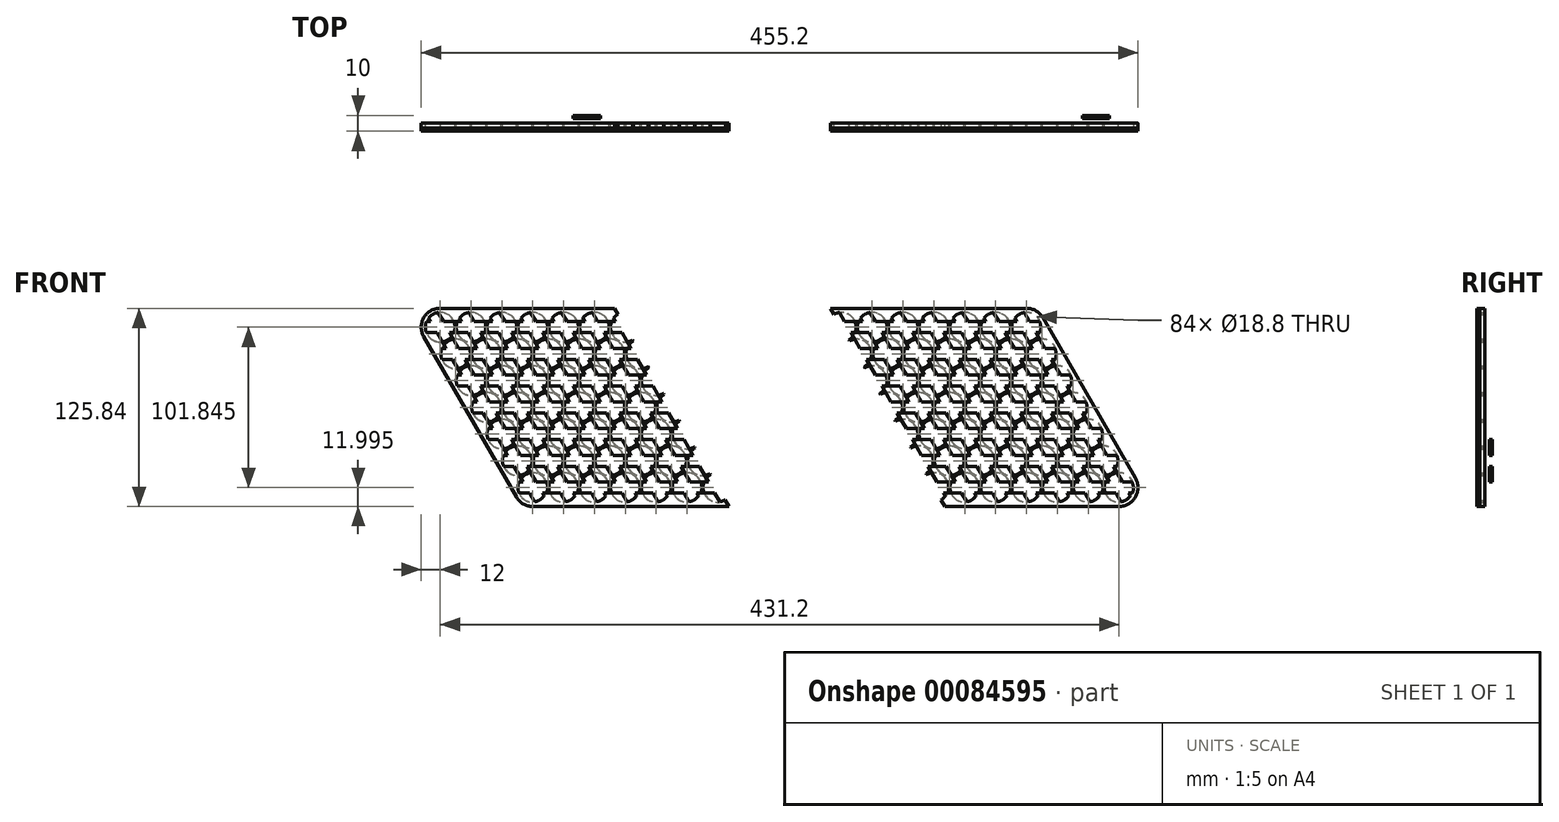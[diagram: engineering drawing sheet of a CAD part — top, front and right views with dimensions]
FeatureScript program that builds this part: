
annotation { "Feature Type Name" : "Feature", "Feature Type Description" : "" }
export const myFeature = defineFeature(function(context is Context, id is Id, definition is map)
    precondition{}
    {
        {
            var Q0;
            Q0=qCreatedBy(makeId("Front.planeOp"),FACE);
            var sketch = newSketch(context, id + "F0", { "sketchPlane" : qUnion([Q0]) });
            skLineSegment(sketch, "E0", {"start": v(0, 0) * mm, "end": v(79.44, 0) * mm, "construction": true});
            skLineSegment(sketch, "E1", {"start": v(0, 0) * mm, "end": v(43.4, -75.16) * mm, "construction": true});
            skCircle(sketch, "E2", {"center": v(0, 0) * mm, "radius": 9.4 * mm});
            skCircle(sketch, "E3.1.0.0", {"center": v(19.6, 0) * mm, "radius": 9.4 * mm});
            skCircle(sketch, "E3.2.0.0", {"center": v(39.2, 0) * mm, "radius": 9.4 * mm});
            skCircle(sketch, "E3.3.0.0", {"center": v(58.8, 0) * mm, "radius": 9.4 * mm});
            skCircle(sketch, "E3.4.0.0", {"center": v(78.4, 0) * mm, "radius": 9.4 * mm});
            skCircle(sketch, "E3.5.0.0", {"center": v(98, 0) * mm, "radius": 9.4 * mm});
            skCircle(sketch, "E3.6.0.0", {"center": v(117.6, 0) * mm, "radius": 9.4 * mm});
            skCircle(sketch, "E3.7.0.0", {"center": v(137.2, 0) * mm, "radius": 9.4 * mm});
            skCircle(sketch, "E3.8.0.0", {"center": v(156.8, 0) * mm, "radius": 9.4 * mm});
            skCircle(sketch, "E3.9.0.0", {"center": v(176.4, 0) * mm, "radius": 9.4 * mm});
            skCircle(sketch, "E3.10.0.0", {"center": v(196, 0) * mm, "radius": 9.4 * mm});
            skCircle(sketch, "E3.11.0.0", {"center": v(215.6, 0) * mm, "radius": 9.4 * mm});
            skCircle(sketch, "E3.12.0.0", {"center": v(235.2, 0) * mm, "radius": 9.4 * mm});
            skCircle(sketch, "E3.13.0.0", {"center": v(254.8, 0) * mm, "radius": 9.4 * mm});
            skCircle(sketch, "E3.14.0.0", {"center": v(274.4, 0) * mm, "radius": 9.4 * mm});
            skCircle(sketch, "E3.15.0.0", {"center": v(294, 0) * mm, "radius": 9.4 * mm});
            skCircle(sketch, "E3.16.0.0", {"center": v(313.6, 0) * mm, "radius": 9.4 * mm});
            skCircle(sketch, "E3.17.0.0", {"center": v(333.2, 0) * mm, "radius": 9.4 * mm});
            skCircle(sketch, "E3.18.0.0", {"center": v(352.8, 0) * mm, "radius": 9.4 * mm});
            skCircle(sketch, "E3.19.0.0", {"center": v(372.4, 0) * mm, "radius": 9.4 * mm});
            skLineSegment(sketch, "E3.direction1", {"start": v(0, 0) * mm, "end": v(19.6, 0) * mm, "construction": true});
            skCircle(sketch, "E4.1.0.0", {"center": v(9.8, -16.97) * mm, "radius": 9.4 * mm});
            skCircle(sketch, "E4.2.0.0", {"center": v(19.6, -33.95) * mm, "radius": 9.4 * mm});
            skCircle(sketch, "E4.3.0.0", {"center": v(29.4, -50.92) * mm, "radius": 9.4 * mm});
            skCircle(sketch, "E4.4.0.0", {"center": v(39.2, -67.9) * mm, "radius": 9.4 * mm});
            skCircle(sketch, "E4.5.0.0", {"center": v(49, -84.87) * mm, "radius": 9.4 * mm});
            skCircle(sketch, "E4.6.0.0", {"center": v(58.8, -101.84) * mm, "radius": 9.4 * mm});
            skLineSegment(sketch, "E4.direction1", {"start": v(0, 0) * mm, "end": v(9.8, -16.97) * mm, "construction": true});
            skCircle(sketch, "E5.1.0.0", {"center": v(29.4, -16.97) * mm, "radius": 9.4 * mm});
            skCircle(sketch, "E5.1.0.1", {"center": v(39.2, -33.95) * mm, "radius": 9.4 * mm});
            skCircle(sketch, "E5.1.0.2", {"center": v(49, -50.92) * mm, "radius": 9.4 * mm});
            skCircle(sketch, "E5.1.0.3", {"center": v(58.8, -67.9) * mm, "radius": 9.4 * mm});
            skCircle(sketch, "E5.1.0.4", {"center": v(68.6, -84.87) * mm, "radius": 9.4 * mm});
            skCircle(sketch, "E5.1.0.5", {"center": v(78.4, -101.84) * mm, "radius": 9.4 * mm});
            skCircle(sketch, "E5.2.0.0", {"center": v(49, -16.97) * mm, "radius": 9.4 * mm});
            skCircle(sketch, "E5.2.0.1", {"center": v(58.8, -33.95) * mm, "radius": 9.4 * mm});
            skCircle(sketch, "E5.2.0.2", {"center": v(68.6, -50.92) * mm, "radius": 9.4 * mm});
            skCircle(sketch, "E5.2.0.3", {"center": v(78.4, -67.9) * mm, "radius": 9.4 * mm});
            skCircle(sketch, "E5.2.0.4", {"center": v(88.2, -84.87) * mm, "radius": 9.4 * mm});
            skCircle(sketch, "E5.2.0.5", {"center": v(98, -101.84) * mm, "radius": 9.4 * mm});
            skCircle(sketch, "E5.3.0.0", {"center": v(68.6, -16.97) * mm, "radius": 9.4 * mm});
            skCircle(sketch, "E5.3.0.1", {"center": v(78.4, -33.95) * mm, "radius": 9.4 * mm});
            skCircle(sketch, "E5.3.0.2", {"center": v(88.2, -50.92) * mm, "radius": 9.4 * mm});
            skCircle(sketch, "E5.3.0.3", {"center": v(98, -67.9) * mm, "radius": 9.4 * mm});
            skCircle(sketch, "E5.3.0.4", {"center": v(107.8, -84.87) * mm, "radius": 9.4 * mm});
            skCircle(sketch, "E5.3.0.5", {"center": v(117.6, -101.84) * mm, "radius": 9.4 * mm});
            skCircle(sketch, "E5.4.0.0", {"center": v(88.2, -16.97) * mm, "radius": 9.4 * mm});
            skCircle(sketch, "E5.4.0.1", {"center": v(98, -33.95) * mm, "radius": 9.4 * mm});
            skCircle(sketch, "E5.4.0.2", {"center": v(107.8, -50.92) * mm, "radius": 9.4 * mm});
            skCircle(sketch, "E5.4.0.3", {"center": v(117.6, -67.9) * mm, "radius": 9.4 * mm});
            skCircle(sketch, "E5.4.0.4", {"center": v(127.4, -84.87) * mm, "radius": 9.4 * mm});
            skCircle(sketch, "E5.4.0.5", {"center": v(137.2, -101.84) * mm, "radius": 9.4 * mm});
            skCircle(sketch, "E5.5.0.0", {"center": v(107.8, -16.97) * mm, "radius": 9.4 * mm});
            skCircle(sketch, "E5.5.0.1", {"center": v(117.6, -33.95) * mm, "radius": 9.4 * mm});
            skCircle(sketch, "E5.5.0.2", {"center": v(127.4, -50.92) * mm, "radius": 9.4 * mm});
            skCircle(sketch, "E5.5.0.3", {"center": v(137.2, -67.9) * mm, "radius": 9.4 * mm});
            skCircle(sketch, "E5.5.0.4", {"center": v(147, -84.87) * mm, "radius": 9.4 * mm});
            skCircle(sketch, "E5.5.0.5", {"center": v(156.8, -101.84) * mm, "radius": 9.4 * mm});
            skCircle(sketch, "E5.6.0.0", {"center": v(127.4, -16.97) * mm, "radius": 9.4 * mm});
            skCircle(sketch, "E5.6.0.1", {"center": v(137.2, -33.95) * mm, "radius": 9.4 * mm});
            skCircle(sketch, "E5.6.0.2", {"center": v(147, -50.92) * mm, "radius": 9.4 * mm});
            skCircle(sketch, "E5.6.0.3", {"center": v(156.8, -67.9) * mm, "radius": 9.4 * mm});
            skCircle(sketch, "E5.6.0.4", {"center": v(166.6, -84.87) * mm, "radius": 9.4 * mm});
            skCircle(sketch, "E5.6.0.5", {"center": v(176.4, -101.84) * mm, "radius": 9.4 * mm});
            skCircle(sketch, "E5.7.0.0", {"center": v(147, -16.97) * mm, "radius": 9.4 * mm});
            skCircle(sketch, "E5.7.0.1", {"center": v(156.8, -33.95) * mm, "radius": 9.4 * mm});
            skCircle(sketch, "E5.7.0.2", {"center": v(166.6, -50.92) * mm, "radius": 9.4 * mm});
            skCircle(sketch, "E5.7.0.3", {"center": v(176.4, -67.9) * mm, "radius": 9.4 * mm});
            skCircle(sketch, "E5.7.0.4", {"center": v(186.2, -84.87) * mm, "radius": 9.4 * mm});
            skCircle(sketch, "E5.7.0.5", {"center": v(196, -101.84) * mm, "radius": 9.4 * mm});
            skCircle(sketch, "E5.8.0.0", {"center": v(166.6, -16.97) * mm, "radius": 9.4 * mm});
            skCircle(sketch, "E5.8.0.1", {"center": v(176.4, -33.95) * mm, "radius": 9.4 * mm});
            skCircle(sketch, "E5.8.0.2", {"center": v(186.2, -50.92) * mm, "radius": 9.4 * mm});
            skCircle(sketch, "E5.8.0.3", {"center": v(196, -67.9) * mm, "radius": 9.4 * mm});
            skCircle(sketch, "E5.8.0.4", {"center": v(205.8, -84.87) * mm, "radius": 9.4 * mm});
            skCircle(sketch, "E5.8.0.5", {"center": v(215.6, -101.84) * mm, "radius": 9.4 * mm});
            skCircle(sketch, "E5.9.0.0", {"center": v(186.2, -16.97) * mm, "radius": 9.4 * mm});
            skCircle(sketch, "E5.9.0.1", {"center": v(196, -33.95) * mm, "radius": 9.4 * mm});
            skCircle(sketch, "E5.9.0.2", {"center": v(205.8, -50.92) * mm, "radius": 9.4 * mm});
            skCircle(sketch, "E5.9.0.3", {"center": v(215.6, -67.9) * mm, "radius": 9.4 * mm});
            skCircle(sketch, "E5.9.0.4", {"center": v(225.4, -84.87) * mm, "radius": 9.4 * mm});
            skCircle(sketch, "E5.9.0.5", {"center": v(235.2, -101.84) * mm, "radius": 9.4 * mm});
            skCircle(sketch, "E5.10.0.0", {"center": v(205.8, -16.97) * mm, "radius": 9.4 * mm});
            skCircle(sketch, "E5.10.0.1", {"center": v(215.6, -33.95) * mm, "radius": 9.4 * mm});
            skCircle(sketch, "E5.10.0.2", {"center": v(225.4, -50.92) * mm, "radius": 9.4 * mm});
            skCircle(sketch, "E5.10.0.3", {"center": v(235.2, -67.9) * mm, "radius": 9.4 * mm});
            skCircle(sketch, "E5.10.0.4", {"center": v(245, -84.87) * mm, "radius": 9.4 * mm});
            skCircle(sketch, "E5.10.0.5", {"center": v(254.8, -101.84) * mm, "radius": 9.4 * mm});
            skCircle(sketch, "E5.11.0.0", {"center": v(225.4, -16.97) * mm, "radius": 9.4 * mm});
            skCircle(sketch, "E5.11.0.1", {"center": v(235.2, -33.95) * mm, "radius": 9.4 * mm});
            skCircle(sketch, "E5.11.0.2", {"center": v(245, -50.92) * mm, "radius": 9.4 * mm});
            skCircle(sketch, "E5.11.0.3", {"center": v(254.8, -67.9) * mm, "radius": 9.4 * mm});
            skCircle(sketch, "E5.11.0.4", {"center": v(264.6, -84.87) * mm, "radius": 9.4 * mm});
            skCircle(sketch, "E5.11.0.5", {"center": v(274.4, -101.84) * mm, "radius": 9.4 * mm});
            skCircle(sketch, "E5.12.0.0", {"center": v(245, -16.97) * mm, "radius": 9.4 * mm});
            skCircle(sketch, "E5.12.0.1", {"center": v(254.8, -33.95) * mm, "radius": 9.4 * mm});
            skCircle(sketch, "E5.12.0.2", {"center": v(264.6, -50.92) * mm, "radius": 9.4 * mm});
            skCircle(sketch, "E5.12.0.3", {"center": v(274.4, -67.9) * mm, "radius": 9.4 * mm});
            skCircle(sketch, "E5.12.0.4", {"center": v(284.2, -84.87) * mm, "radius": 9.4 * mm});
            skCircle(sketch, "E5.12.0.5", {"center": v(294, -101.84) * mm, "radius": 9.4 * mm});
            skCircle(sketch, "E5.13.0.0", {"center": v(264.6, -16.97) * mm, "radius": 9.4 * mm});
            skCircle(sketch, "E5.13.0.1", {"center": v(274.4, -33.95) * mm, "radius": 9.4 * mm});
            skCircle(sketch, "E5.13.0.2", {"center": v(284.2, -50.92) * mm, "radius": 9.4 * mm});
            skCircle(sketch, "E5.13.0.3", {"center": v(294, -67.9) * mm, "radius": 9.4 * mm});
            skCircle(sketch, "E5.13.0.4", {"center": v(303.8, -84.87) * mm, "radius": 9.4 * mm});
            skCircle(sketch, "E5.13.0.5", {"center": v(313.6, -101.84) * mm, "radius": 9.4 * mm});
            skCircle(sketch, "E5.14.0.0", {"center": v(284.2, -16.97) * mm, "radius": 9.4 * mm});
            skCircle(sketch, "E5.14.0.1", {"center": v(294, -33.95) * mm, "radius": 9.4 * mm});
            skCircle(sketch, "E5.14.0.2", {"center": v(303.8, -50.92) * mm, "radius": 9.4 * mm});
            skCircle(sketch, "E5.14.0.3", {"center": v(313.6, -67.9) * mm, "radius": 9.4 * mm});
            skCircle(sketch, "E5.14.0.4", {"center": v(323.4, -84.87) * mm, "radius": 9.4 * mm});
            skCircle(sketch, "E5.14.0.5", {"center": v(333.2, -101.84) * mm, "radius": 9.4 * mm});
            skCircle(sketch, "E5.15.0.0", {"center": v(303.8, -16.97) * mm, "radius": 9.4 * mm});
            skCircle(sketch, "E5.15.0.1", {"center": v(313.6, -33.95) * mm, "radius": 9.4 * mm});
            skCircle(sketch, "E5.15.0.2", {"center": v(323.4, -50.92) * mm, "radius": 9.4 * mm});
            skCircle(sketch, "E5.15.0.3", {"center": v(333.2, -67.9) * mm, "radius": 9.4 * mm});
            skCircle(sketch, "E5.15.0.4", {"center": v(343, -84.87) * mm, "radius": 9.4 * mm});
            skCircle(sketch, "E5.15.0.5", {"center": v(352.8, -101.84) * mm, "radius": 9.4 * mm});
            skCircle(sketch, "E5.16.0.0", {"center": v(323.4, -16.97) * mm, "radius": 9.4 * mm});
            skCircle(sketch, "E5.16.0.1", {"center": v(333.2, -33.95) * mm, "radius": 9.4 * mm});
            skCircle(sketch, "E5.16.0.2", {"center": v(343, -50.92) * mm, "radius": 9.4 * mm});
            skCircle(sketch, "E5.16.0.3", {"center": v(352.8, -67.9) * mm, "radius": 9.4 * mm});
            skCircle(sketch, "E5.16.0.4", {"center": v(362.6, -84.87) * mm, "radius": 9.4 * mm});
            skCircle(sketch, "E5.16.0.5", {"center": v(372.4, -101.84) * mm, "radius": 9.4 * mm});
            skCircle(sketch, "E5.17.0.0", {"center": v(343, -16.97) * mm, "radius": 9.4 * mm});
            skCircle(sketch, "E5.17.0.1", {"center": v(352.8, -33.95) * mm, "radius": 9.4 * mm});
            skCircle(sketch, "E5.17.0.2", {"center": v(362.6, -50.92) * mm, "radius": 9.4 * mm});
            skCircle(sketch, "E5.17.0.3", {"center": v(372.4, -67.9) * mm, "radius": 9.4 * mm});
            skCircle(sketch, "E5.17.0.4", {"center": v(382.2, -84.87) * mm, "radius": 9.4 * mm});
            skCircle(sketch, "E5.17.0.5", {"center": v(392, -101.84) * mm, "radius": 9.4 * mm});
            skCircle(sketch, "E5.18.0.0", {"center": v(362.6, -16.97) * mm, "radius": 9.4 * mm});
            skCircle(sketch, "E5.18.0.1", {"center": v(372.4, -33.95) * mm, "radius": 9.4 * mm});
            skCircle(sketch, "E5.18.0.2", {"center": v(382.2, -50.92) * mm, "radius": 9.4 * mm});
            skCircle(sketch, "E5.18.0.3", {"center": v(392, -67.9) * mm, "radius": 9.4 * mm});
            skCircle(sketch, "E5.18.0.4", {"center": v(401.8, -84.87) * mm, "radius": 9.4 * mm});
            skCircle(sketch, "E5.18.0.5", {"center": v(411.6, -101.84) * mm, "radius": 9.4 * mm});
            skCircle(sketch, "E5.19.0.0", {"center": v(382.2, -16.97) * mm, "radius": 9.4 * mm});
            skCircle(sketch, "E5.19.0.1", {"center": v(392, -33.95) * mm, "radius": 9.4 * mm});
            skCircle(sketch, "E5.19.0.2", {"center": v(401.8, -50.92) * mm, "radius": 9.4 * mm});
            skCircle(sketch, "E5.19.0.3", {"center": v(411.6, -67.9) * mm, "radius": 9.4 * mm});
            skCircle(sketch, "E5.19.0.4", {"center": v(421.4, -84.87) * mm, "radius": 9.4 * mm});
            skCircle(sketch, "E5.19.0.5", {"center": v(431.2, -101.84) * mm, "radius": 9.4 * mm});
            skLineSegment(sketch, "E5.direction1", {"start": v(9.8, -16.97) * mm, "end": v(29.4, -16.97) * mm, "construction": true});
            skLineSegment(sketch, "E6", {"start": v(0, 0) * mm, "end": v(372.4, 0) * mm, "construction": true});
            skLineSegment(sketch, "E7", {"start": v(372.4, 0) * mm, "end": v(441, -118.82) * mm, "construction": true});
            skLineSegment(sketch, "E8", {"start": v(441, -118.82) * mm, "end": v(68.6, -118.82) * mm, "construction": true});
            skLineSegment(sketch, "E9", {"start": v(68.6, -118.82) * mm, "end": v(0, 0) * mm, "construction": true});
            skArc(sketch, "E10", {"start": v(48.4, -107.84) * mm, "mid": v(52.8, -112.24) * mm, "end": v(58.8, -113.84) * mm});
            skArc(sketch, "E11", {"start": v(431.2, -113.84) * mm, "mid": v(441.6, -107.84) * mm, "end": v(441.6, -95.84) * mm});
            skArc(sketch, "E12", {"start": v(382.8, 6) * mm, "mid": v(378.4, 10.4) * mm, "end": v(372.4, 12) * mm});
            skArc(sketch, "E13", {"start": v(0, 12) * mm, "mid": v(-10.4, 6) * mm, "end": v(-10.4, -6) * mm});
            skLineSegment(sketch, "E14", {"start": v(0, 12) * mm, "end": v(372.4, 12) * mm});
            skLineSegment(sketch, "E15", {"start": v(-10.4, -6) * mm, "end": v(48.4, -107.84) * mm});
            skLineSegment(sketch, "E16", {"start": v(58.8, -113.84) * mm, "end": v(431.2, -113.84) * mm});
            skLineSegment(sketch, "E17", {"start": v(441.6, -95.84) * mm, "end": v(382.8, 6) * mm});
            skLineSegment(sketch, "E18", {"start": v(441.6, -107.84) * mm, "end": v(500.4, -6) * mm, "construction": true});
            skLineSegment(sketch, "E19", {"start": v(372.4, 12) * mm, "end": v(490, 12) * mm, "construction": true});
            skPoint(sketch, "E20.visualSharp", {"position": v(510.78, 12) * mm});
            skArc(sketch, "E20.filletArc", {"start": v(500.4, -6) * mm, "mid": v(500.4, 6) * mm, "end": v(490, 12) * mm, "construction": true});
            skSolve(sketch);
        }
        {
            var Q0;
            Q0=makeQuery(id+"F0.imprint","IMPRINT",FACE,{"disambiguationData":[TD([[makeQuery(id+"F0.imprint","IMPRINT",EDGE,{"derivedFrom":sQuery(id+"F0.wireOp",EDGE,"E2")}),-1.0]])]});
            extrude(context, id + "F1", {"entities" : qUnion([Q0]), "depth" : 3 * mm});
        }
        {
            var Q0;
            Q0=makeQuery(id+"F1.opExtrude","CAP_FACE",FACE,{"disambiguationData":[OSD([sQuery(id+"F0.wireOp",EDGE,"E2"),sQuery(id+"F0.wireOp",EDGE,"E3.1.0.0"),sQuery(id+"F0.wireOp",EDGE,"E3.2.0.0"),sQuery(id+"F0.wireOp",EDGE,"E3.3.0.0"),sQuery(id+"F0.wireOp",EDGE,"E3.4.0.0"),sQuery(id+"F0.wireOp",EDGE,"E3.5.0.0"),sQuery(id+"F0.wireOp",EDGE,"E3.6.0.0"),sQuery(id+"F0.wireOp",EDGE,"E3.7.0.0"),sQuery(id+"F0.wireOp",EDGE,"E3.8.0.0"),sQuery(id+"F0.wireOp",EDGE,"E3.9.0.0"),sQuery(id+"F0.wireOp",EDGE,"E3.10.0.0"),sQuery(id+"F0.wireOp",EDGE,"E3.11.0.0"),sQuery(id+"F0.wireOp",EDGE,"E3.12.0.0"),sQuery(id+"F0.wireOp",EDGE,"E3.13.0.0"),sQuery(id+"F0.wireOp",EDGE,"E3.14.0.0"),sQuery(id+"F0.wireOp",EDGE,"E3.15.0.0"),sQuery(id+"F0.wireOp",EDGE,"E3.16.0.0"),sQuery(id+"F0.wireOp",EDGE,"E3.17.0.0"),sQuery(id+"F0.wireOp",EDGE,"E3.18.0.0"),sQuery(id+"F0.wireOp",EDGE,"E3.19.0.0"),sQuery(id+"F0.wireOp",EDGE,"E4.1.0.0"),sQuery(id+"F0.wireOp",EDGE,"E4.2.0.0"),sQuery(id+"F0.wireOp",EDGE,"E4.3.0.0"),sQuery(id+"F0.wireOp",EDGE,"E4.4.0.0"),sQuery(id+"F0.wireOp",EDGE,"E4.5.0.0"),sQuery(id+"F0.wireOp",EDGE,"E4.6.0.0"),sQuery(id+"F0.wireOp",EDGE,"E5.1.0.0"),sQuery(id+"F0.wireOp",EDGE,"E5.1.0.1"),sQuery(id+"F0.wireOp",EDGE,"E5.1.0.2"),sQuery(id+"F0.wireOp",EDGE,"E5.1.0.3"),sQuery(id+"F0.wireOp",EDGE,"E5.1.0.4"),sQuery(id+"F0.wireOp",EDGE,"E5.1.0.5"),sQuery(id+"F0.wireOp",EDGE,"E5.2.0.0"),sQuery(id+"F0.wireOp",EDGE,"E5.2.0.1"),sQuery(id+"F0.wireOp",EDGE,"E5.2.0.2"),sQuery(id+"F0.wireOp",EDGE,"E5.2.0.3"),sQuery(id+"F0.wireOp",EDGE,"E5.2.0.4"),sQuery(id+"F0.wireOp",EDGE,"E5.2.0.5"),sQuery(id+"F0.wireOp",EDGE,"E5.3.0.0"),sQuery(id+"F0.wireOp",EDGE,"E5.3.0.1"),sQuery(id+"F0.wireOp",EDGE,"E5.3.0.2"),sQuery(id+"F0.wireOp",EDGE,"E5.3.0.3"),sQuery(id+"F0.wireOp",EDGE,"E5.3.0.4"),sQuery(id+"F0.wireOp",EDGE,"E5.3.0.5"),sQuery(id+"F0.wireOp",EDGE,"E5.4.0.0"),sQuery(id+"F0.wireOp",EDGE,"E5.4.0.1"),sQuery(id+"F0.wireOp",EDGE,"E5.4.0.2"),sQuery(id+"F0.wireOp",EDGE,"E5.4.0.3"),sQuery(id+"F0.wireOp",EDGE,"E5.4.0.4"),sQuery(id+"F0.wireOp",EDGE,"E5.4.0.5"),sQuery(id+"F0.wireOp",EDGE,"E5.5.0.0"),sQuery(id+"F0.wireOp",EDGE,"E5.5.0.1"),sQuery(id+"F0.wireOp",EDGE,"E5.5.0.2"),sQuery(id+"F0.wireOp",EDGE,"E5.5.0.3"),sQuery(id+"F0.wireOp",EDGE,"E5.5.0.4"),sQuery(id+"F0.wireOp",EDGE,"E5.5.0.5"),sQuery(id+"F0.wireOp",EDGE,"E5.6.0.0"),sQuery(id+"F0.wireOp",EDGE,"E5.6.0.1"),sQuery(id+"F0.wireOp",EDGE,"E5.6.0.2"),sQuery(id+"F0.wireOp",EDGE,"E5.6.0.3"),sQuery(id+"F0.wireOp",EDGE,"E5.6.0.4"),sQuery(id+"F0.wireOp",EDGE,"E5.6.0.5"),sQuery(id+"F0.wireOp",EDGE,"E5.7.0.0"),sQuery(id+"F0.wireOp",EDGE,"E5.7.0.1"),sQuery(id+"F0.wireOp",EDGE,"E5.7.0.2"),sQuery(id+"F0.wireOp",EDGE,"E5.7.0.3"),sQuery(id+"F0.wireOp",EDGE,"E5.7.0.4"),sQuery(id+"F0.wireOp",EDGE,"E5.7.0.5"),sQuery(id+"F0.wireOp",EDGE,"E5.8.0.0"),sQuery(id+"F0.wireOp",EDGE,"E5.8.0.1"),sQuery(id+"F0.wireOp",EDGE,"E5.8.0.2"),sQuery(id+"F0.wireOp",EDGE,"E5.8.0.3"),sQuery(id+"F0.wireOp",EDGE,"E5.8.0.4"),sQuery(id+"F0.wireOp",EDGE,"E5.8.0.5"),sQuery(id+"F0.wireOp",EDGE,"E5.9.0.0"),sQuery(id+"F0.wireOp",EDGE,"E5.9.0.1"),sQuery(id+"F0.wireOp",EDGE,"E5.9.0.2"),sQuery(id+"F0.wireOp",EDGE,"E5.9.0.3"),sQuery(id+"F0.wireOp",EDGE,"E5.9.0.4"),sQuery(id+"F0.wireOp",EDGE,"E5.9.0.5"),sQuery(id+"F0.wireOp",EDGE,"E5.10.0.0"),sQuery(id+"F0.wireOp",EDGE,"E5.10.0.1"),sQuery(id+"F0.wireOp",EDGE,"E5.10.0.2"),sQuery(id+"F0.wireOp",EDGE,"E5.10.0.3"),sQuery(id+"F0.wireOp",EDGE,"E5.10.0.4"),sQuery(id+"F0.wireOp",EDGE,"E5.10.0.5"),sQuery(id+"F0.wireOp",EDGE,"E5.11.0.0"),sQuery(id+"F0.wireOp",EDGE,"E5.11.0.1"),sQuery(id+"F0.wireOp",EDGE,"E5.11.0.2"),sQuery(id+"F0.wireOp",EDGE,"E5.11.0.3"),sQuery(id+"F0.wireOp",EDGE,"E5.11.0.4"),sQuery(id+"F0.wireOp",EDGE,"E5.11.0.5"),sQuery(id+"F0.wireOp",EDGE,"E5.12.0.0"),sQuery(id+"F0.wireOp",EDGE,"E5.12.0.1"),sQuery(id+"F0.wireOp",EDGE,"E5.12.0.2"),sQuery(id+"F0.wireOp",EDGE,"E5.12.0.3"),sQuery(id+"F0.wireOp",EDGE,"E5.12.0.4"),sQuery(id+"F0.wireOp",EDGE,"E5.12.0.5"),sQuery(id+"F0.wireOp",EDGE,"E5.13.0.0"),sQuery(id+"F0.wireOp",EDGE,"E5.13.0.1"),sQuery(id+"F0.wireOp",EDGE,"E5.13.0.2"),sQuery(id+"F0.wireOp",EDGE,"E5.13.0.3"),sQuery(id+"F0.wireOp",EDGE,"E5.13.0.4"),sQuery(id+"F0.wireOp",EDGE,"E5.13.0.5"),sQuery(id+"F0.wireOp",EDGE,"E5.14.0.0"),sQuery(id+"F0.wireOp",EDGE,"E5.14.0.1"),sQuery(id+"F0.wireOp",EDGE,"E5.14.0.2"),sQuery(id+"F0.wireOp",EDGE,"E5.14.0.3"),sQuery(id+"F0.wireOp",EDGE,"E5.14.0.4"),sQuery(id+"F0.wireOp",EDGE,"E5.14.0.5"),sQuery(id+"F0.wireOp",EDGE,"E5.15.0.0"),sQuery(id+"F0.wireOp",EDGE,"E5.15.0.1"),sQuery(id+"F0.wireOp",EDGE,"E5.15.0.2"),sQuery(id+"F0.wireOp",EDGE,"E5.15.0.3"),sQuery(id+"F0.wireOp",EDGE,"E5.15.0.4"),sQuery(id+"F0.wireOp",EDGE,"E5.15.0.5"),sQuery(id+"F0.wireOp",EDGE,"E5.16.0.0"),sQuery(id+"F0.wireOp",EDGE,"E5.16.0.1"),sQuery(id+"F0.wireOp",EDGE,"E5.16.0.2"),sQuery(id+"F0.wireOp",EDGE,"E5.16.0.3"),sQuery(id+"F0.wireOp",EDGE,"E5.16.0.4"),sQuery(id+"F0.wireOp",EDGE,"E5.16.0.5"),sQuery(id+"F0.wireOp",EDGE,"E5.17.0.0"),sQuery(id+"F0.wireOp",EDGE,"E5.17.0.1"),sQuery(id+"F0.wireOp",EDGE,"E5.17.0.2"),sQuery(id+"F0.wireOp",EDGE,"E5.17.0.3"),sQuery(id+"F0.wireOp",EDGE,"E5.17.0.4"),sQuery(id+"F0.wireOp",EDGE,"E5.17.0.5"),sQuery(id+"F0.wireOp",EDGE,"E5.18.0.0"),sQuery(id+"F0.wireOp",EDGE,"E5.18.0.1"),sQuery(id+"F0.wireOp",EDGE,"E5.18.0.2"),sQuery(id+"F0.wireOp",EDGE,"E5.18.0.3"),sQuery(id+"F0.wireOp",EDGE,"E5.18.0.4"),sQuery(id+"F0.wireOp",EDGE,"E5.18.0.5"),sQuery(id+"F0.wireOp",EDGE,"E5.19.0.0"),sQuery(id+"F0.wireOp",EDGE,"E5.19.0.1"),sQuery(id+"F0.wireOp",EDGE,"E5.19.0.2"),sQuery(id+"F0.wireOp",EDGE,"E5.19.0.3"),sQuery(id+"F0.wireOp",EDGE,"E5.19.0.4"),sQuery(id+"F0.wireOp",EDGE,"E5.19.0.5"),sQuery(id+"F0.wireOp",EDGE,"E10"),sQuery(id+"F0.wireOp",EDGE,"E11"),sQuery(id+"F0.wireOp",EDGE,"E12"),sQuery(id+"F0.wireOp",EDGE,"E13"),sQuery(id+"F0.wireOp",EDGE,"E14"),sQuery(id+"F0.wireOp",EDGE,"E15"),sQuery(id+"F0.wireOp",EDGE,"E16"),sQuery(id+"F0.wireOp",EDGE,"E17")])],"isStart":false});
            var sketch = newSketch(context, id + "F2", { "sketchPlane" : qUnion([Q0]) });
            skLineSegment(sketch, "E21.0", {"start": v(0, 12) * mm, "end": v(372.4, 12) * mm});
            skArc(sketch, "E21.1", {"start": v(0, 12) * mm, "mid": v(-10.4, 6) * mm, "end": v(-10.4, -6) * mm});
            skLineSegment(sketch, "E21.2", {"start": v(-10.4, -6) * mm, "end": v(48.4, -107.84) * mm});
            skArc(sketch, "E21.3", {"start": v(382.8, 6) * mm, "mid": v(378.4, 10.4) * mm, "end": v(372.4, 12) * mm});
            skLineSegment(sketch, "E21.4", {"start": v(441.6, -95.84) * mm, "end": v(382.8, 6) * mm});
            skArc(sketch, "E21.5", {"start": v(431.2, -113.84) * mm, "mid": v(441.6, -107.84) * mm, "end": v(441.6, -95.84) * mm});
            skLineSegment(sketch, "E21.6", {"start": v(58.8, -113.84) * mm, "end": v(431.2, -113.84) * mm});
            skArc(sketch, "E21.7", {"start": v(48.4, -107.84) * mm, "mid": v(52.8, -112.24) * mm, "end": v(58.8, -113.84) * mm});
            skSolve(sketch);
        }
        {
            var Q0;
            Q0=qSketchRegion(id+"F2",true);
            extrude(context, id + "F3", {"entities" : qUnion([Q0]), "depth" : 2 * mm});
        }
        {
            var Q0;
            Q0=makeQuery(id+"F3.opExtrude","CAP_FACE",FACE,{"disambiguationData":[OSD([sQuery(id+"F2.wireOp",EDGE,"E21.0"),sQuery(id+"F2.wireOp",EDGE,"E21.1"),sQuery(id+"F2.wireOp",EDGE,"E21.2"),sQuery(id+"F2.wireOp",EDGE,"E21.3"),sQuery(id+"F2.wireOp",EDGE,"E21.4"),sQuery(id+"F2.wireOp",EDGE,"E21.5"),sQuery(id+"F2.wireOp",EDGE,"E21.6"),sQuery(id+"F2.wireOp",EDGE,"E21.7")])],"isStart":false});
            var sketch = newSketch(context, id + "F4", { "sketchPlane" : qUnion([Q0]) });
            skLineSegment(sketch, "E22", {"start": v(0, 0) * mm, "end": v(58.8, -101.84) * mm, "construction": true});
            skLineSegment(sketch, "E23", {"start": v(58.8, -101.84) * mm, "end": v(431.2, -101.84) * mm, "construction": true});
            skLineSegment(sketch, "E24", {"start": v(431.2, -101.84) * mm, "end": v(372.4, 0) * mm, "construction": true});
            skLineSegment(sketch, "E25", {"start": v(372.4, 0) * mm, "end": v(0, 0) * mm, "construction": true});
            skLineSegment(sketch, "E26", {"start": v(-8.72, 3.5) * mm, "end": v(380.69, 3.5) * mm});
            skLineSegment(sketch, "E27.MirrorCS", {"start": v(-8.72, -3.5) * mm, "end": v(380.9, -3.5) * mm});
            skArc(sketch, "E28.0", {"start": v(-8.72, 3.5) * mm, "mid": v(-9.4, 0) * mm, "end": v(-8.72, -3.5) * mm});
            skArc(sketch, "E29.trimOffspring", {"start": v(380.9, -3.5) * mm, "mid": v(381.47, 0.02) * mm, "end": v(380.69, 3.5) * mm});
            skPoint(sketch, "E30.orphan", {"position": v(456.43, 3.5) * mm});
            skPoint(sketch, "E31.orphan", {"position": v(456.43, -3.5) * mm});
            skPoint(sketch, "E32.orphan", {"position": v(-45.25, 3.5) * mm});
            skPoint(sketch, "E33.orphan", {"position": v(-45.25, -3.5) * mm});
            skLineSegment(sketch, "E34.0.1.0", {"start": v(1.08, -13.47) * mm, "end": v(390.49, -13.47) * mm});
            skLineSegment(sketch, "E34.0.1.1", {"start": v(1.08, -20.47) * mm, "end": v(390.7, -20.47) * mm});
            skArc(sketch, "E34.0.1.2", {"start": v(1.08, -13.47) * mm, "mid": v(0.4, -16.97) * mm, "end": v(1.08, -20.47) * mm});
            skArc(sketch, "E34.0.1.3", {"start": v(390.7, -20.47) * mm, "mid": v(391.27, -16.95) * mm, "end": v(390.49, -13.47) * mm});
            skLineSegment(sketch, "E34.0.2.0", {"start": v(10.88, -30.45) * mm, "end": v(400.29, -30.45) * mm});
            skLineSegment(sketch, "E34.0.2.1", {"start": v(10.88, -37.45) * mm, "end": v(400.5, -37.45) * mm});
            skArc(sketch, "E34.0.2.2", {"start": v(10.88, -30.45) * mm, "mid": v(10.2, -33.95) * mm, "end": v(10.88, -37.45) * mm});
            skArc(sketch, "E34.0.2.3", {"start": v(400.5, -37.45) * mm, "mid": v(401.07, -33.93) * mm, "end": v(400.29, -30.45) * mm});
            skLineSegment(sketch, "E34.0.3.0", {"start": v(20.68, -47.42) * mm, "end": v(410.09, -47.42) * mm});
            skLineSegment(sketch, "E34.0.3.1", {"start": v(20.68, -54.42) * mm, "end": v(410.3, -54.42) * mm});
            skArc(sketch, "E34.0.3.2", {"start": v(20.68, -47.42) * mm, "mid": v(20, -50.92) * mm, "end": v(20.68, -54.42) * mm});
            skArc(sketch, "E34.0.3.3", {"start": v(410.3, -54.42) * mm, "mid": v(410.87, -50.9) * mm, "end": v(410.09, -47.42) * mm});
            skLineSegment(sketch, "E34.0.4.0", {"start": v(30.48, -64.4) * mm, "end": v(419.89, -64.4) * mm});
            skLineSegment(sketch, "E34.0.4.1", {"start": v(30.48, -71.4) * mm, "end": v(420.1, -71.4) * mm});
            skArc(sketch, "E34.0.4.2", {"start": v(30.48, -64.4) * mm, "mid": v(29.8, -67.9) * mm, "end": v(30.48, -71.4) * mm});
            skArc(sketch, "E34.0.4.3", {"start": v(420.1, -71.4) * mm, "mid": v(420.67, -67.88) * mm, "end": v(419.89, -64.4) * mm});
            skLineSegment(sketch, "E34.0.5.0", {"start": v(40.28, -81.37) * mm, "end": v(429.69, -81.37) * mm});
            skLineSegment(sketch, "E34.0.5.1", {"start": v(40.28, -88.37) * mm, "end": v(429.9, -88.37) * mm});
            skArc(sketch, "E34.0.5.2", {"start": v(40.28, -81.37) * mm, "mid": v(39.6, -84.87) * mm, "end": v(40.28, -88.37) * mm});
            skArc(sketch, "E34.0.5.3", {"start": v(429.9, -88.37) * mm, "mid": v(430.47, -84.85) * mm, "end": v(429.69, -81.37) * mm});
            skLineSegment(sketch, "E34.0.6.0", {"start": v(50.08, -98.34) * mm, "end": v(439.49, -98.34) * mm});
            skLineSegment(sketch, "E34.0.6.1", {"start": v(50.08, -105.34) * mm, "end": v(439.7, -105.34) * mm});
            skArc(sketch, "E34.0.6.2", {"start": v(50.08, -98.34) * mm, "mid": v(49.4, -101.84) * mm, "end": v(50.08, -105.34) * mm});
            skArc(sketch, "E34.0.6.3", {"start": v(439.7, -105.34) * mm, "mid": v(440.27, -101.82) * mm, "end": v(439.49, -98.34) * mm});
            skLineSegment(sketch, "E34.direction1", {"start": v(-8.72, 3.5) * mm, "end": v(16.28, 3.5) * mm, "construction": true});
            skLineSegment(sketch, "E34.direction2", {"start": v(-8.72, 3.5) * mm, "end": v(1.08, -13.47) * mm, "construction": true});
            skSolve(sketch);
        }
        {
            var Q0;
            Q0=qSketchRegion(id+"F4",true);
            extrude(context, id + "F5", {"entities" : qUnion([Q0]), "operationType" : NewBodyOperationType.REMOVE, "endBound" : BoundingType.UP_TO_NEXT, "oppositeDirection" : true, "depth" : 25 * mm});
        }
        {
            var Q0;
            Q0=makeQuery(id+"F3.opExtrude","CAP_FACE",FACE,{"disambiguationData":[OSD([sQuery(id+"F2.wireOp",EDGE,"E21.0"),sQuery(id+"F2.wireOp",EDGE,"E21.1"),sQuery(id+"F2.wireOp",EDGE,"E21.2"),sQuery(id+"F2.wireOp",EDGE,"E21.3"),sQuery(id+"F2.wireOp",EDGE,"E21.4"),sQuery(id+"F2.wireOp",EDGE,"E21.5"),sQuery(id+"F2.wireOp",EDGE,"E21.6"),sQuery(id+"F2.wireOp",EDGE,"E21.7")])],"isStart":false});
            var sketch = newSketch(context, id + "F6", { "sketchPlane" : qUnion([Q0]) });
            skLineSegment(sketch, "E35", {"start": v(0, 0) * mm, "end": v(58.8, -101.84) * mm, "construction": true});
            skLineSegment(sketch, "E36", {"start": v(-1.33, 9.3) * mm, "end": v(65.94, -107.21) * mm});
            skLineSegment(sketch, "E37.MirrorCS", {"start": v(-7.4, 5.8) * mm, "end": v(60.02, -110.96) * mm});
            skArc(sketch, "E38.0", {"start": v(-1.33, 9.3) * mm, "mid": v(-4.7, 8.14) * mm, "end": v(-7.4, 5.8) * mm});
            skArc(sketch, "E39.trimOffspring", {"start": v(60.02, -110.96) * mm, "mid": v(63.34, -109.66) * mm, "end": v(65.94, -107.21) * mm});
            skPoint(sketch, "E40.orphan", {"position": v(72.39, -132.38) * mm});
            skPoint(sketch, "E41.orphan", {"position": v(78.45, -128.88) * mm});
            skPoint(sketch, "E42.orphan", {"position": v(-7.3, 19.64) * mm});
            skPoint(sketch, "E43.orphan", {"position": v(-13.36, 16.14) * mm});
            skArc(sketch, "E44.1.0.0", {"start": v(18.27, 9.3) * mm, "mid": v(14.9, 8.14) * mm, "end": v(12.2, 5.8) * mm});
            skLineSegment(sketch, "E44.1.0.1", {"start": v(12.2, 5.8) * mm, "end": v(79.62, -110.96) * mm});
            skLineSegment(sketch, "E44.1.0.2", {"start": v(18.27, 9.3) * mm, "end": v(85.54, -107.21) * mm});
            skArc(sketch, "E44.1.0.3", {"start": v(79.62, -110.96) * mm, "mid": v(82.94, -109.66) * mm, "end": v(85.54, -107.21) * mm});
            skArc(sketch, "E44.2.0.0", {"start": v(37.87, 9.3) * mm, "mid": v(34.5, 8.14) * mm, "end": v(31.8, 5.8) * mm});
            skLineSegment(sketch, "E44.2.0.1", {"start": v(31.8, 5.8) * mm, "end": v(99.22, -110.96) * mm});
            skLineSegment(sketch, "E44.2.0.2", {"start": v(37.87, 9.3) * mm, "end": v(105.14, -107.21) * mm});
            skArc(sketch, "E44.2.0.3", {"start": v(99.22, -110.96) * mm, "mid": v(102.54, -109.66) * mm, "end": v(105.14, -107.21) * mm});
            skArc(sketch, "E44.3.0.0", {"start": v(57.47, 9.3) * mm, "mid": v(54.1, 8.14) * mm, "end": v(51.4, 5.8) * mm});
            skLineSegment(sketch, "E44.3.0.1", {"start": v(51.4, 5.8) * mm, "end": v(118.82, -110.96) * mm});
            skLineSegment(sketch, "E44.3.0.2", {"start": v(57.47, 9.3) * mm, "end": v(124.74, -107.21) * mm});
            skArc(sketch, "E44.3.0.3", {"start": v(118.82, -110.96) * mm, "mid": v(122.14, -109.66) * mm, "end": v(124.74, -107.21) * mm});
            skArc(sketch, "E44.4.0.0", {"start": v(77.07, 9.3) * mm, "mid": v(73.7, 8.14) * mm, "end": v(71, 5.8) * mm});
            skLineSegment(sketch, "E44.4.0.1", {"start": v(71, 5.8) * mm, "end": v(138.42, -110.96) * mm});
            skLineSegment(sketch, "E44.4.0.2", {"start": v(77.07, 9.3) * mm, "end": v(144.34, -107.21) * mm});
            skArc(sketch, "E44.4.0.3", {"start": v(138.42, -110.96) * mm, "mid": v(141.74, -109.66) * mm, "end": v(144.34, -107.21) * mm});
            skArc(sketch, "E44.5.0.0", {"start": v(96.67, 9.3) * mm, "mid": v(93.3, 8.14) * mm, "end": v(90.6, 5.8) * mm});
            skLineSegment(sketch, "E44.5.0.1", {"start": v(90.6, 5.8) * mm, "end": v(158.02, -110.96) * mm});
            skLineSegment(sketch, "E44.5.0.2", {"start": v(96.67, 9.3) * mm, "end": v(163.94, -107.21) * mm});
            skArc(sketch, "E44.5.0.3", {"start": v(158.02, -110.96) * mm, "mid": v(161.34, -109.66) * mm, "end": v(163.94, -107.21) * mm});
            skArc(sketch, "E44.6.0.0", {"start": v(116.27, 9.3) * mm, "mid": v(112.9, 8.14) * mm, "end": v(110.2, 5.8) * mm});
            skLineSegment(sketch, "E44.6.0.1", {"start": v(110.2, 5.8) * mm, "end": v(177.62, -110.96) * mm});
            skLineSegment(sketch, "E44.6.0.2", {"start": v(116.27, 9.3) * mm, "end": v(183.54, -107.21) * mm});
            skArc(sketch, "E44.6.0.3", {"start": v(177.62, -110.96) * mm, "mid": v(180.94, -109.66) * mm, "end": v(183.54, -107.21) * mm});
            skArc(sketch, "E44.7.0.0", {"start": v(135.87, 9.3) * mm, "mid": v(132.5, 8.14) * mm, "end": v(129.8, 5.8) * mm});
            skLineSegment(sketch, "E44.7.0.1", {"start": v(129.8, 5.8) * mm, "end": v(197.22, -110.96) * mm});
            skLineSegment(sketch, "E44.7.0.2", {"start": v(135.87, 9.3) * mm, "end": v(203.14, -107.21) * mm});
            skArc(sketch, "E44.7.0.3", {"start": v(197.22, -110.96) * mm, "mid": v(200.54, -109.66) * mm, "end": v(203.14, -107.21) * mm});
            skArc(sketch, "E44.8.0.0", {"start": v(155.47, 9.3) * mm, "mid": v(152.1, 8.14) * mm, "end": v(149.4, 5.8) * mm});
            skLineSegment(sketch, "E44.8.0.1", {"start": v(149.4, 5.8) * mm, "end": v(216.82, -110.96) * mm});
            skLineSegment(sketch, "E44.8.0.2", {"start": v(155.47, 9.3) * mm, "end": v(222.74, -107.21) * mm});
            skArc(sketch, "E44.8.0.3", {"start": v(216.82, -110.96) * mm, "mid": v(220.14, -109.66) * mm, "end": v(222.74, -107.21) * mm});
            skArc(sketch, "E44.9.0.0", {"start": v(175.07, 9.3) * mm, "mid": v(171.7, 8.14) * mm, "end": v(169, 5.8) * mm});
            skLineSegment(sketch, "E44.9.0.1", {"start": v(169, 5.8) * mm, "end": v(236.42, -110.96) * mm});
            skLineSegment(sketch, "E44.9.0.2", {"start": v(175.07, 9.3) * mm, "end": v(242.34, -107.21) * mm});
            skArc(sketch, "E44.9.0.3", {"start": v(236.42, -110.96) * mm, "mid": v(239.74, -109.66) * mm, "end": v(242.34, -107.21) * mm});
            skArc(sketch, "E44.10.0.0", {"start": v(194.67, 9.3) * mm, "mid": v(191.3, 8.14) * mm, "end": v(188.6, 5.8) * mm});
            skLineSegment(sketch, "E44.10.0.1", {"start": v(188.6, 5.8) * mm, "end": v(256.02, -110.96) * mm});
            skLineSegment(sketch, "E44.10.0.2", {"start": v(194.67, 9.3) * mm, "end": v(261.94, -107.21) * mm});
            skArc(sketch, "E44.10.0.3", {"start": v(256.02, -110.96) * mm, "mid": v(259.34, -109.66) * mm, "end": v(261.94, -107.21) * mm});
            skArc(sketch, "E44.11.0.0", {"start": v(214.27, 9.3) * mm, "mid": v(210.9, 8.14) * mm, "end": v(208.2, 5.8) * mm});
            skLineSegment(sketch, "E44.11.0.1", {"start": v(208.2, 5.8) * mm, "end": v(275.62, -110.96) * mm});
            skLineSegment(sketch, "E44.11.0.2", {"start": v(214.27, 9.3) * mm, "end": v(281.54, -107.21) * mm});
            skArc(sketch, "E44.11.0.3", {"start": v(275.62, -110.96) * mm, "mid": v(278.94, -109.66) * mm, "end": v(281.54, -107.21) * mm});
            skArc(sketch, "E44.12.0.0", {"start": v(233.87, 9.3) * mm, "mid": v(230.5, 8.14) * mm, "end": v(227.8, 5.8) * mm});
            skLineSegment(sketch, "E44.12.0.1", {"start": v(227.8, 5.8) * mm, "end": v(295.22, -110.96) * mm});
            skLineSegment(sketch, "E44.12.0.2", {"start": v(233.87, 9.3) * mm, "end": v(301.14, -107.21) * mm});
            skArc(sketch, "E44.12.0.3", {"start": v(295.22, -110.96) * mm, "mid": v(298.54, -109.66) * mm, "end": v(301.14, -107.21) * mm});
            skArc(sketch, "E44.13.0.0", {"start": v(253.47, 9.3) * mm, "mid": v(250.1, 8.14) * mm, "end": v(247.4, 5.8) * mm});
            skLineSegment(sketch, "E44.13.0.1", {"start": v(247.4, 5.8) * mm, "end": v(314.82, -110.96) * mm});
            skLineSegment(sketch, "E44.13.0.2", {"start": v(253.47, 9.3) * mm, "end": v(320.74, -107.21) * mm});
            skArc(sketch, "E44.13.0.3", {"start": v(314.82, -110.96) * mm, "mid": v(318.14, -109.66) * mm, "end": v(320.74, -107.21) * mm});
            skArc(sketch, "E44.14.0.0", {"start": v(273.07, 9.3) * mm, "mid": v(269.7, 8.14) * mm, "end": v(267, 5.8) * mm});
            skLineSegment(sketch, "E44.14.0.1", {"start": v(267, 5.8) * mm, "end": v(334.42, -110.96) * mm});
            skLineSegment(sketch, "E44.14.0.2", {"start": v(273.07, 9.3) * mm, "end": v(340.34, -107.21) * mm});
            skArc(sketch, "E44.14.0.3", {"start": v(334.42, -110.96) * mm, "mid": v(337.74, -109.66) * mm, "end": v(340.34, -107.21) * mm});
            skArc(sketch, "E44.15.0.0", {"start": v(292.67, 9.3) * mm, "mid": v(289.3, 8.14) * mm, "end": v(286.6, 5.8) * mm});
            skLineSegment(sketch, "E44.15.0.1", {"start": v(286.6, 5.8) * mm, "end": v(354.02, -110.96) * mm});
            skLineSegment(sketch, "E44.15.0.2", {"start": v(292.67, 9.3) * mm, "end": v(359.94, -107.21) * mm});
            skArc(sketch, "E44.15.0.3", {"start": v(354.02, -110.96) * mm, "mid": v(357.34, -109.66) * mm, "end": v(359.94, -107.21) * mm});
            skArc(sketch, "E44.16.0.0", {"start": v(312.27, 9.3) * mm, "mid": v(308.9, 8.14) * mm, "end": v(306.2, 5.8) * mm});
            skLineSegment(sketch, "E44.16.0.1", {"start": v(306.2, 5.8) * mm, "end": v(373.62, -110.96) * mm});
            skLineSegment(sketch, "E44.16.0.2", {"start": v(312.27, 9.3) * mm, "end": v(379.54, -107.21) * mm});
            skArc(sketch, "E44.16.0.3", {"start": v(373.62, -110.96) * mm, "mid": v(376.94, -109.66) * mm, "end": v(379.54, -107.21) * mm});
            skArc(sketch, "E44.17.0.0", {"start": v(331.87, 9.3) * mm, "mid": v(328.5, 8.14) * mm, "end": v(325.8, 5.8) * mm});
            skLineSegment(sketch, "E44.17.0.1", {"start": v(325.8, 5.8) * mm, "end": v(393.22, -110.96) * mm});
            skLineSegment(sketch, "E44.17.0.2", {"start": v(331.87, 9.3) * mm, "end": v(399.14, -107.21) * mm});
            skArc(sketch, "E44.17.0.3", {"start": v(393.22, -110.96) * mm, "mid": v(396.54, -109.66) * mm, "end": v(399.14, -107.21) * mm});
            skArc(sketch, "E44.18.0.0", {"start": v(351.47, 9.3) * mm, "mid": v(348.1, 8.14) * mm, "end": v(345.4, 5.8) * mm});
            skLineSegment(sketch, "E44.18.0.1", {"start": v(345.4, 5.8) * mm, "end": v(412.82, -110.96) * mm});
            skLineSegment(sketch, "E44.18.0.2", {"start": v(351.47, 9.3) * mm, "end": v(418.74, -107.21) * mm});
            skArc(sketch, "E44.18.0.3", {"start": v(412.82, -110.96) * mm, "mid": v(416.14, -109.66) * mm, "end": v(418.74, -107.21) * mm});
            skArc(sketch, "E44.19.0.0", {"start": v(371.07, 9.3) * mm, "mid": v(367.7, 8.14) * mm, "end": v(365, 5.8) * mm});
            skLineSegment(sketch, "E44.19.0.1", {"start": v(365, 5.8) * mm, "end": v(432.42, -110.96) * mm});
            skLineSegment(sketch, "E44.19.0.2", {"start": v(371.07, 9.3) * mm, "end": v(438.34, -107.21) * mm});
            skArc(sketch, "E44.19.0.3", {"start": v(432.42, -110.96) * mm, "mid": v(435.74, -109.66) * mm, "end": v(438.34, -107.21) * mm});
            skLineSegment(sketch, "E44.direction1", {"start": v(-7.4, 5.8) * mm, "end": v(12.2, 5.8) * mm, "construction": true});
            skSolve(sketch);
        }
        {
            var Q0;
            Q0=qSketchRegion(id+"F6",true);
            extrude(context, id + "F7", {"entities" : qUnion([Q0]), "operationType" : NewBodyOperationType.REMOVE, "oppositeDirection" : true, "depth" : 2 * mm});
        }
        {
            var Q0;
            Q0=makeQuery(id+"F1.opExtrude","CAP_FACE",FACE,{"disambiguationData":[OSD([sQuery(id+"F0.wireOp",EDGE,"E2"),sQuery(id+"F0.wireOp",EDGE,"E3.1.0.0"),sQuery(id+"F0.wireOp",EDGE,"E3.2.0.0"),sQuery(id+"F0.wireOp",EDGE,"E3.3.0.0"),sQuery(id+"F0.wireOp",EDGE,"E3.4.0.0"),sQuery(id+"F0.wireOp",EDGE,"E3.5.0.0"),sQuery(id+"F0.wireOp",EDGE,"E3.6.0.0"),sQuery(id+"F0.wireOp",EDGE,"E3.7.0.0"),sQuery(id+"F0.wireOp",EDGE,"E3.8.0.0"),sQuery(id+"F0.wireOp",EDGE,"E3.9.0.0"),sQuery(id+"F0.wireOp",EDGE,"E3.10.0.0"),sQuery(id+"F0.wireOp",EDGE,"E3.11.0.0"),sQuery(id+"F0.wireOp",EDGE,"E3.12.0.0"),sQuery(id+"F0.wireOp",EDGE,"E3.13.0.0"),sQuery(id+"F0.wireOp",EDGE,"E3.14.0.0"),sQuery(id+"F0.wireOp",EDGE,"E3.15.0.0"),sQuery(id+"F0.wireOp",EDGE,"E3.16.0.0"),sQuery(id+"F0.wireOp",EDGE,"E3.17.0.0"),sQuery(id+"F0.wireOp",EDGE,"E3.18.0.0"),sQuery(id+"F0.wireOp",EDGE,"E3.19.0.0"),sQuery(id+"F0.wireOp",EDGE,"E4.1.0.0"),sQuery(id+"F0.wireOp",EDGE,"E4.2.0.0"),sQuery(id+"F0.wireOp",EDGE,"E4.3.0.0"),sQuery(id+"F0.wireOp",EDGE,"E4.4.0.0"),sQuery(id+"F0.wireOp",EDGE,"E4.5.0.0"),sQuery(id+"F0.wireOp",EDGE,"E4.6.0.0"),sQuery(id+"F0.wireOp",EDGE,"E5.1.0.0"),sQuery(id+"F0.wireOp",EDGE,"E5.1.0.1"),sQuery(id+"F0.wireOp",EDGE,"E5.1.0.2"),sQuery(id+"F0.wireOp",EDGE,"E5.1.0.3"),sQuery(id+"F0.wireOp",EDGE,"E5.1.0.4"),sQuery(id+"F0.wireOp",EDGE,"E5.1.0.5"),sQuery(id+"F0.wireOp",EDGE,"E5.2.0.0"),sQuery(id+"F0.wireOp",EDGE,"E5.2.0.1"),sQuery(id+"F0.wireOp",EDGE,"E5.2.0.2"),sQuery(id+"F0.wireOp",EDGE,"E5.2.0.3"),sQuery(id+"F0.wireOp",EDGE,"E5.2.0.4"),sQuery(id+"F0.wireOp",EDGE,"E5.2.0.5"),sQuery(id+"F0.wireOp",EDGE,"E5.3.0.0"),sQuery(id+"F0.wireOp",EDGE,"E5.3.0.1"),sQuery(id+"F0.wireOp",EDGE,"E5.3.0.2"),sQuery(id+"F0.wireOp",EDGE,"E5.3.0.3"),sQuery(id+"F0.wireOp",EDGE,"E5.3.0.4"),sQuery(id+"F0.wireOp",EDGE,"E5.3.0.5"),sQuery(id+"F0.wireOp",EDGE,"E5.4.0.0"),sQuery(id+"F0.wireOp",EDGE,"E5.4.0.1"),sQuery(id+"F0.wireOp",EDGE,"E5.4.0.2"),sQuery(id+"F0.wireOp",EDGE,"E5.4.0.3"),sQuery(id+"F0.wireOp",EDGE,"E5.4.0.4"),sQuery(id+"F0.wireOp",EDGE,"E5.4.0.5"),sQuery(id+"F0.wireOp",EDGE,"E5.5.0.0"),sQuery(id+"F0.wireOp",EDGE,"E5.5.0.1"),sQuery(id+"F0.wireOp",EDGE,"E5.5.0.2"),sQuery(id+"F0.wireOp",EDGE,"E5.5.0.3"),sQuery(id+"F0.wireOp",EDGE,"E5.5.0.4"),sQuery(id+"F0.wireOp",EDGE,"E5.5.0.5"),sQuery(id+"F0.wireOp",EDGE,"E5.6.0.0"),sQuery(id+"F0.wireOp",EDGE,"E5.6.0.1"),sQuery(id+"F0.wireOp",EDGE,"E5.6.0.2"),sQuery(id+"F0.wireOp",EDGE,"E5.6.0.3"),sQuery(id+"F0.wireOp",EDGE,"E5.6.0.4"),sQuery(id+"F0.wireOp",EDGE,"E5.6.0.5"),sQuery(id+"F0.wireOp",EDGE,"E5.7.0.0"),sQuery(id+"F0.wireOp",EDGE,"E5.7.0.1"),sQuery(id+"F0.wireOp",EDGE,"E5.7.0.2"),sQuery(id+"F0.wireOp",EDGE,"E5.7.0.3"),sQuery(id+"F0.wireOp",EDGE,"E5.7.0.4"),sQuery(id+"F0.wireOp",EDGE,"E5.7.0.5"),sQuery(id+"F0.wireOp",EDGE,"E5.8.0.0"),sQuery(id+"F0.wireOp",EDGE,"E5.8.0.1"),sQuery(id+"F0.wireOp",EDGE,"E5.8.0.2"),sQuery(id+"F0.wireOp",EDGE,"E5.8.0.3"),sQuery(id+"F0.wireOp",EDGE,"E5.8.0.4"),sQuery(id+"F0.wireOp",EDGE,"E5.8.0.5"),sQuery(id+"F0.wireOp",EDGE,"E5.9.0.0"),sQuery(id+"F0.wireOp",EDGE,"E5.9.0.1"),sQuery(id+"F0.wireOp",EDGE,"E5.9.0.2"),sQuery(id+"F0.wireOp",EDGE,"E5.9.0.3"),sQuery(id+"F0.wireOp",EDGE,"E5.9.0.4"),sQuery(id+"F0.wireOp",EDGE,"E5.9.0.5"),sQuery(id+"F0.wireOp",EDGE,"E5.10.0.0"),sQuery(id+"F0.wireOp",EDGE,"E5.10.0.1"),sQuery(id+"F0.wireOp",EDGE,"E5.10.0.2"),sQuery(id+"F0.wireOp",EDGE,"E5.10.0.3"),sQuery(id+"F0.wireOp",EDGE,"E5.10.0.4"),sQuery(id+"F0.wireOp",EDGE,"E5.10.0.5"),sQuery(id+"F0.wireOp",EDGE,"E5.11.0.0"),sQuery(id+"F0.wireOp",EDGE,"E5.11.0.1"),sQuery(id+"F0.wireOp",EDGE,"E5.11.0.2"),sQuery(id+"F0.wireOp",EDGE,"E5.11.0.3"),sQuery(id+"F0.wireOp",EDGE,"E5.11.0.4"),sQuery(id+"F0.wireOp",EDGE,"E5.11.0.5"),sQuery(id+"F0.wireOp",EDGE,"E5.12.0.0"),sQuery(id+"F0.wireOp",EDGE,"E5.12.0.1"),sQuery(id+"F0.wireOp",EDGE,"E5.12.0.2"),sQuery(id+"F0.wireOp",EDGE,"E5.12.0.3"),sQuery(id+"F0.wireOp",EDGE,"E5.12.0.4"),sQuery(id+"F0.wireOp",EDGE,"E5.12.0.5"),sQuery(id+"F0.wireOp",EDGE,"E5.13.0.0"),sQuery(id+"F0.wireOp",EDGE,"E5.13.0.1"),sQuery(id+"F0.wireOp",EDGE,"E5.13.0.2"),sQuery(id+"F0.wireOp",EDGE,"E5.13.0.3"),sQuery(id+"F0.wireOp",EDGE,"E5.13.0.4"),sQuery(id+"F0.wireOp",EDGE,"E5.13.0.5"),sQuery(id+"F0.wireOp",EDGE,"E5.14.0.0"),sQuery(id+"F0.wireOp",EDGE,"E5.14.0.1"),sQuery(id+"F0.wireOp",EDGE,"E5.14.0.2"),sQuery(id+"F0.wireOp",EDGE,"E5.14.0.3"),sQuery(id+"F0.wireOp",EDGE,"E5.14.0.4"),sQuery(id+"F0.wireOp",EDGE,"E5.14.0.5"),sQuery(id+"F0.wireOp",EDGE,"E5.15.0.0"),sQuery(id+"F0.wireOp",EDGE,"E5.15.0.1"),sQuery(id+"F0.wireOp",EDGE,"E5.15.0.2"),sQuery(id+"F0.wireOp",EDGE,"E5.15.0.3"),sQuery(id+"F0.wireOp",EDGE,"E5.15.0.4"),sQuery(id+"F0.wireOp",EDGE,"E5.15.0.5"),sQuery(id+"F0.wireOp",EDGE,"E5.16.0.0"),sQuery(id+"F0.wireOp",EDGE,"E5.16.0.1"),sQuery(id+"F0.wireOp",EDGE,"E5.16.0.2"),sQuery(id+"F0.wireOp",EDGE,"E5.16.0.3"),sQuery(id+"F0.wireOp",EDGE,"E5.16.0.4"),sQuery(id+"F0.wireOp",EDGE,"E5.16.0.5"),sQuery(id+"F0.wireOp",EDGE,"E5.17.0.0"),sQuery(id+"F0.wireOp",EDGE,"E5.17.0.1"),sQuery(id+"F0.wireOp",EDGE,"E5.17.0.2"),sQuery(id+"F0.wireOp",EDGE,"E5.17.0.3"),sQuery(id+"F0.wireOp",EDGE,"E5.17.0.4"),sQuery(id+"F0.wireOp",EDGE,"E5.17.0.5"),sQuery(id+"F0.wireOp",EDGE,"E5.18.0.0"),sQuery(id+"F0.wireOp",EDGE,"E5.18.0.1"),sQuery(id+"F0.wireOp",EDGE,"E5.18.0.2"),sQuery(id+"F0.wireOp",EDGE,"E5.18.0.3"),sQuery(id+"F0.wireOp",EDGE,"E5.18.0.4"),sQuery(id+"F0.wireOp",EDGE,"E5.18.0.5"),sQuery(id+"F0.wireOp",EDGE,"E5.19.0.0"),sQuery(id+"F0.wireOp",EDGE,"E5.19.0.1"),sQuery(id+"F0.wireOp",EDGE,"E5.19.0.2"),sQuery(id+"F0.wireOp",EDGE,"E5.19.0.3"),sQuery(id+"F0.wireOp",EDGE,"E5.19.0.4"),sQuery(id+"F0.wireOp",EDGE,"E5.19.0.5"),sQuery(id+"F0.wireOp",EDGE,"E10"),sQuery(id+"F0.wireOp",EDGE,"E11"),sQuery(id+"F0.wireOp",EDGE,"E12"),sQuery(id+"F0.wireOp",EDGE,"E13"),sQuery(id+"F0.wireOp",EDGE,"E14"),sQuery(id+"F0.wireOp",EDGE,"E15"),sQuery(id+"F0.wireOp",EDGE,"E16"),sQuery(id+"F0.wireOp",EDGE,"E17")])],"isStart":true});
            var sketch = newSketch(context, id + "F8", { "sketchPlane" : qUnion([Q0]) });
            skCircle(sketch, "E45.0", {"center": v(-117.6, 0) * mm, "radius": 9.4 * mm, "construction": true});
            skCircle(sketch, "E45.2", {"center": v(-313.6, -101.84) * mm, "radius": 9.4 * mm, "construction": true});
            skCircle(sketch, "E45.3", {"center": v(-254.8, 0) * mm, "radius": 9.4 * mm, "construction": true});
            skCircle(sketch, "E46.0", {"center": v(-176.4, -101.84) * mm, "radius": 9.4 * mm, "construction": true});
            skLineSegment(sketch, "E47", {"start": v(-117.6, 0) * mm, "end": v(-176.4, -101.84) * mm});
            skLineSegment(sketch, "E48", {"start": v(-176.4, -101.84) * mm, "end": v(-189.42, -124.4) * mm});
            skLineSegment(sketch, "E49", {"start": v(-117.6, 0) * mm, "end": v(-104.55, 22.6) * mm});
            skLineSegment(sketch, "E50", {"start": v(-313.6, -101.84) * mm, "end": v(-254.8, 0) * mm});
            skLineSegment(sketch, "E51", {"start": v(-254.8, 0) * mm, "end": v(-241.75, 22.6) * mm});
            skLineSegment(sketch, "E52", {"start": v(-313.6, -101.84) * mm, "end": v(-326.17, -123.62) * mm});
            skLineSegment(sketch, "E53", {"start": v(-189.42, -124.4) * mm, "end": v(-326.62, -124.4) * mm});
            skLineSegment(sketch, "E54", {"start": v(-104.55, 22.6) * mm, "end": v(-241.75, 22.6) * mm});
            skLineSegment(sketch, "E55", {"start": v(-326.17, -123.62) * mm, "end": v(-326.62, -124.4) * mm});
            skSolve(sketch);
        }
        {
            var Q0;
            Q0 = qSketchRegion(id + "F8", true);
            extrude(context, id + "F9", {"entities" : qUnion([Q0]), "operationType" : NewBodyOperationType.REMOVE, "oppositeDirection" : true, "depth" : 50 * mm});
        }
        {
            var Q0;
            Q0=makeQuery(id+"F7.boolean.opBoolean","SPLIT",BODY,{"disambiguationData":[OD(79.0)],"derivedFrom":makeQuery(id+"F3.opExtrude","SWEPT_BODY",BODY,{"disambiguationData":[OSD([sQuery(id+"F2.wireOp",EDGE,"E21.0"),sQuery(id+"F2.wireOp",EDGE,"E21.1"),sQuery(id+"F2.wireOp",EDGE,"E21.2"),sQuery(id+"F2.wireOp",EDGE,"E21.3"),sQuery(id+"F2.wireOp",EDGE,"E21.4"),sQuery(id+"F2.wireOp",EDGE,"E21.5"),sQuery(id+"F2.wireOp",EDGE,"E21.6"),sQuery(id+"F2.wireOp",EDGE,"E21.7")])]})});
            var Q1;
            Q1=makeQuery(id+"F7.boolean.opBoolean","SPLIT",BODY,{"disambiguationData":[OD(114.0)],"derivedFrom":makeQuery(id+"F3.opExtrude","SWEPT_BODY",BODY,{"disambiguationData":[OSD([sQuery(id+"F2.wireOp",EDGE,"E21.0"),sQuery(id+"F2.wireOp",EDGE,"E21.1"),sQuery(id+"F2.wireOp",EDGE,"E21.2"),sQuery(id+"F2.wireOp",EDGE,"E21.3"),sQuery(id+"F2.wireOp",EDGE,"E21.4"),sQuery(id+"F2.wireOp",EDGE,"E21.5"),sQuery(id+"F2.wireOp",EDGE,"E21.6"),sQuery(id+"F2.wireOp",EDGE,"E21.7")])]})});
            var Q2;
            Q2=qCreatedBy(makeId("Front.planeOp"),FACE);
            mirror(context, id + "F10", {"entities" : qUnion([Q0, Q1]), "mirrorPlane" : qUnion([Q2])});
        }
    });
